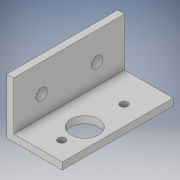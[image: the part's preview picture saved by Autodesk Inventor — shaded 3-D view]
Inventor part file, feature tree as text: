
AUTODESK INVENTOR PART (.ipt)
format: ipt  version: 2018 (Build 220112000, 112)  size: 137,728 bytes
history: native  units: in
note: dims shown in document units (in); Inventor stores cm internally (conversion verified against a paired STEP export)
features: extrude x4, sketch x4
ambient origin geometry x8: Origin, YZ Plane, XZ Plane, XY Plane, X Axis, Y Axis, Z Axis, Center Point
bodies: Solid1 (feature_tree)
feature tree (8):
  extrude  "Extrusion1"  Depth=1.0in
  extrude  "Extrusion2"  Depth=0.125in
  extrude  "Extrusion3"  Depth=2.0in
  extrude  "Extrusion4"  TaperAngle=90.0deg  [1 undecoded]
  sketch  "Sketch1"  dims[d0=0.125in d1=1.0in]
  sketch  "Sketch2"  dims[d2=1.0in d3=0.125in]
  sketch  "Sketch3"  dims[d4=2.0in d5=0.0in d6=0.655in]
  sketch  "Sketch4"  dims[d7=0.75in d8=90.0deg d9=0.5in d10=2.0in d11=0.0in d12=0.413in d13=1.122in d14=0.134in d15=0.134in d16=2.0in d17=0.0in d18=0.5in d19=0.5in d20=1.0in d21=0.2031in d22=2.0in d23=0.0in]
note: 1 required parameter value undecoded (feature->parameter linkage not recoverable at this tier; creation-order binding heuristic only, values carry confidence <= 0.55)
